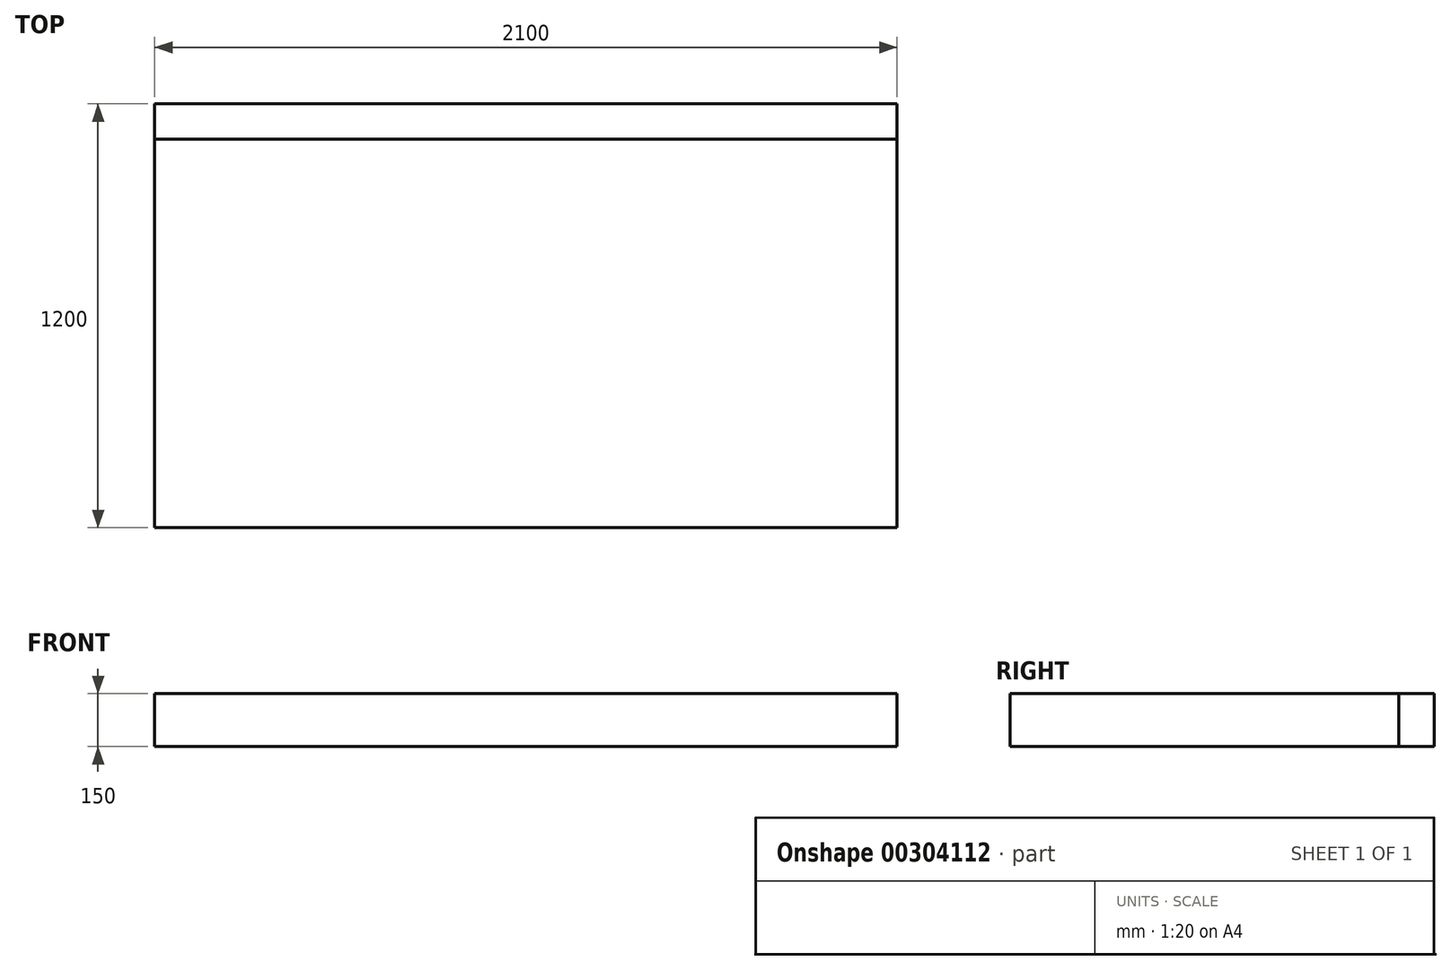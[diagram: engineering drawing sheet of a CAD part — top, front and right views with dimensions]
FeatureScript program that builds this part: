
annotation { "Feature Type Name" : "Feature", "Feature Type Description" : "" }
export const myFeature = defineFeature(function(context is Context, id is Id, definition is map)
    precondition{}
    {
        {
            var Q0;
            Q0=qCreatedBy(makeId("Top.planeOp"),FACE);
            var sketch = newSketch(context, id + "F0", { "sketchPlane" : qUnion([Q0])});
            skLineSegment(sketch, "E0.bottom", {"start": v(-849.49, 503.15) * mm, "end": v(1250.51, 503.15) * mm});
            skLineSegment(sketch, "E0.top", {"start": v(-849.49, -596.85) * mm, "end": v(1250.51, -596.85) * mm});
            skLineSegment(sketch, "E0.left", {"start": v(-849.49, 503.15) * mm, "end": v(-849.49, -596.85) * mm});
            skLineSegment(sketch, "E0.right", {"start": v(1250.51, 503.15) * mm, "end": v(1250.51, -596.85) * mm});
            skSolve(sketch);
        }
        {
            var Q0;
            Q0=makeQuery(id+"F0.imprint","IMPRINT",FACE,{"disambiguationData":[TD([[makeQuery(id+"F0.imprint","IMPRINT",EDGE,{"derivedFrom":sQuery(id+"F0.wireOp",EDGE,"E0.bottom")}),-1.0]])]});
            extrude(context, id + "F1", {"entities" : qUnion([Q0]), "depth" : 150 * mm, "offsetDistance" : 25 * mm});
        }
        {
            var Q0;
            Q0=makeQuery(id+"F1.opExtrude","SWEPT_FACE",FACE,{"disambiguationData":[OSD([sQuery(id+"F0.wireOp",EDGE,"E0.bottom")])]});
            extrude(context, id + "F2", {"entities" : qUnion([Q0]), "depth" : 100 * mm, "offsetDistance" : 25 * mm});
        }
    });
